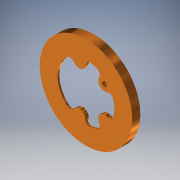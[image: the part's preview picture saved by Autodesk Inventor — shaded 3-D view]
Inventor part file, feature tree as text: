
AUTODESK INVENTOR PART (.ipt)
format: ipt  version: 2017 (Build 210142000, 142)  size: 215,040 bytes
history: native  units: in
note: dims shown in document units (in); Inventor stores cm internally (conversion verified against a paired STEP export)
features: reference x16, extrude x4, sketch x4, other x4, plane x2, fillet x1
ambient origin geometry x8: Origin, YZ Plane, XZ Plane, XY Plane, X Axis, Y Axis, Z Axis, Center Point
bodies: Solid1 (feature_tree)
feature tree (31):
  plane  "Work Plane1"
  extrude  "Extrusion1"  Depth=0.105in
  extrude  "Extrusion2"  Depth=0.01in
  extrude  "Extrusion3"  Depth=0.05in
  sketch  "Sketch4"  dims[d9=0.05in d10=0.175in d11=0.0in d12=0.1in]
  plane  "Work Plane2"
  extrude  "Extrusion4"  Depth=0.1in TaperAngle=0.0deg
  fillet  "Fillet1"  Radius=0.1in
  sketch  "Sketch1"  dims[d0=0.05in d1=0.0in d2=0.105in]
  reference  "Reference1"
  reference  "Reference2"
  reference  "Reference3"
  reference  "Reference4"
  reference  "Reference5"
  sketch  "Sketch2"  dims[d3=0.05in d4=0.0in d5=0.01in]
  reference  "Reference6"
  reference  "Reference7"
  sketch  "Sketch3"  dims[d6=0.175in d7=0.0in d8=0.05in]
  reference  "Reference8"
  reference  "Reference9"
  reference  "Reference10"
  reference  "Reference11"
  reference  "Reference12"
  reference  "Reference13"
  reference  "Reference14"
  reference  "Reference15"
  reference  "Reference16"
  other  "<userpath>\Documents\Inventor\PixyCam and Gimbal\Assembly2.iam"
  other  "Assembly2.iam"
  other  "Ring Front:1"
  other  "LEDRing:1"
